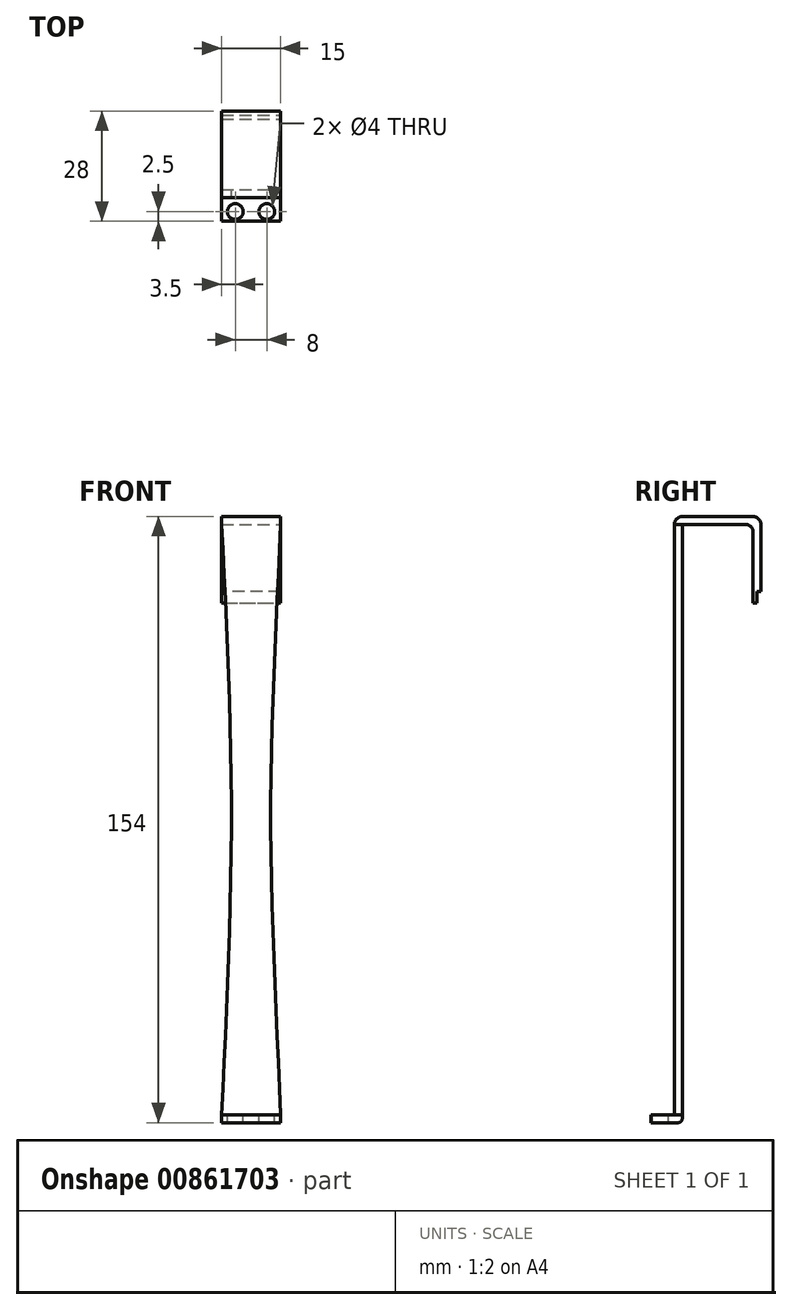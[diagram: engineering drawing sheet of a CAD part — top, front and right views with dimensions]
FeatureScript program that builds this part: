
annotation { "Feature Type Name" : "Feature", "Feature Type Description" : "" }
export const myFeature = defineFeature(function(context is Context, id is Id, definition is map)
    precondition{}
    {
        {
            var Q0;
            Q0=qCreatedBy(makeId("Front.planeOp"),FACE);
            var sketch = newSketch(context, id + "F0", { "sketchPlane" : qUnion([Q0])});
            skLineSegment(sketch, "E0.bottom", {"start": v(-7.5, 72.7) * mm, "end": v(7.5, 72.7) * mm});
            skLineSegment(sketch, "E0.top", {"start": v(-7.5, -77.3) * mm, "end": v(7.5, -77.3) * mm});
            skFitSpline(sketch, "E1", {"points": [v(-7.5, 72.7) * mm, v(-5, 0) * mm, v(-7.5, -77.3) * mm], "startDerivative": vector(7.76, -146.53) * mm, "endDerivative": vector(-7.68, -153.44) * mm});
            skFitSpline(sketch, "E2", {"points": [v(7.5, 72.7) * mm, v(5, 0) * mm, v(7.5, -77.3) * mm], "startDerivative": vector(-6.19, -146.53) * mm, "endDerivative": vector(6.12, -153.44) * mm});
            skSolve(sketch);
        }
        {
            var Q0;
            Q0 = qSketchRegion(id + "F0", true);
            extrude(context, id + "F1", {"entities" : qUnion([Q0]), "depth" : 2 * mm, "offsetDistance" : 25 * mm});
        }
        {
            var Q0;
            Q0=makeQuery(id+"F1.opExtrude","CAP_EDGE",EDGE,{"disambiguationData":[OSD([sQuery(id+"F0.wireOp",EDGE,"E0.bottom")])],"isStart":true});
            var Q1;
            Q1=makeQuery(id+"F1.opExtrude","CAP_EDGE",EDGE,{"disambiguationData":[OSD([sQuery(id+"F0.wireOp",EDGE,"E0.bottom")])],"isStart":false});
            cPlane(context, id + "F2", {"entities" : qUnion([Q0, Q1]), "cplaneType" : CPlaneType.LINE_ANGLE, "offset" : 25 * mm, "angle" : 0 * degree, "width" : 150 * mm, "height" : 150 * mm});
        }
        {
            var Q0;
            Q0=qCreatedBy(id+"F2.planeOp",FACE);
            var sketch = newSketch(context, id + "F3", { "sketchPlane" : qUnion([Q0])});
            skLineSegment(sketch, "E3.bottom", {"start": v(-7.5, -20) * mm, "end": v(7.5, -20) * mm});
            skLineSegment(sketch, "E3.top", {"start": v(-7.5, 2) * mm, "end": v(7.5, 2) * mm});
            skLineSegment(sketch, "E3.left", {"start": v(-7.5, -20) * mm, "end": v(-7.5, 2) * mm});
            skLineSegment(sketch, "E3.right", {"start": v(7.5, -20) * mm, "end": v(7.5, 2) * mm});
            skSolve(sketch);
        }
        {
            var Q0;
            Q0 = qSketchRegion(id + "F3", true);
            extrude(context, id + "F4", {"entities" : qUnion([Q0]), "operationType" : NewBodyOperationType.ADD, "oppositeDirection" : true, "depth" : 2 * mm, "offsetDistance" : 25 * mm});
        }
        {
            var Q0;
            Q0=makeQuery(id+"F4.opExtrude","CAP_EDGE",EDGE,{"disambiguationData":[OSD([sQuery(id+"F3.wireOp",EDGE,"E3.bottom")])],"isStart":false});
            var Q1;
            Q1=makeQuery(id+"F4.opExtrude","CAP_EDGE",EDGE,{"disambiguationData":[OSD([sQuery(id+"F3.wireOp",EDGE,"E3.bottom")])],"isStart":true});
            cPlane(context, id + "F5", {"entities" : qUnion([Q0, Q1]), "cplaneType" : CPlaneType.LINE_ANGLE, "offset" : 25 * mm, "angle" : 0 * degree, "width" : 150 * mm, "height" : 150 * mm});
        }
        {
            var Q0;
            Q0=qCreatedBy(id+"F5.planeOp",FACE);
            var sketch = newSketch(context, id + "F6", { "sketchPlane" : qUnion([Q0])});
            skLineSegment(sketch, "E4.bottom", {"start": v(7.5, 74.7) * mm, "end": v(-7.5, 74.7) * mm});
            skLineSegment(sketch, "E4.top", {"start": v(7.5, 52.7) * mm, "end": v(-7.5, 52.7) * mm});
            skLineSegment(sketch, "E4.left", {"start": v(7.5, 74.7) * mm, "end": v(7.5, 52.7) * mm});
            skLineSegment(sketch, "E4.right", {"start": v(-7.5, 74.7) * mm, "end": v(-7.5, 52.7) * mm});
            skSolve(sketch);
        }
        {
            var Q0;
            Q0 = qSketchRegion(id + "F6", true);
            extrude(context, id + "F7", {"entities" : qUnion([Q0]), "operationType" : NewBodyOperationType.ADD, "oppositeDirection" : true, "depth" : 2 * mm, "offsetDistance" : 25 * mm});
        }
        {
            var Q0;
            Q0=makeQuery(id+"F4.opExtrude","CAP_EDGE",EDGE,{"disambiguationData":[OSD([sQuery(id+"F3.wireOp",EDGE,"E3.top")])],"isStart":false});
            var Q1;
            Q1=makeQuery(id+"F4.opExtrude","CAP_EDGE",EDGE,{"disambiguationData":[OSD([sQuery(id+"F3.wireOp",EDGE,"E3.bottom")])],"isStart":false});
            var Q2;
            Q2=makeQuery(id+"F1.opExtrude","CAP_EDGE",EDGE,{"disambiguationData":[OSD([sQuery(id+"F0.wireOp",EDGE,"E0.bottom")])],"isStart":true});
            var Q3;
            Q3=makeQuery(id+"F7.boolean.opBoolean","INTERSECT",EDGE,{"derivedFrom":[makeQuery(id+"F4.opExtrude","CAP_FACE",FACE,{"disambiguationData":[OSD([sQuery(id+"F3.wireOp",EDGE,"E3.bottom"),sQuery(id+"F3.wireOp",EDGE,"E3.top"),sQuery(id+"F3.wireOp",EDGE,"E3.left"),sQuery(id+"F3.wireOp",EDGE,"E3.right")])],"isStart":true}),makeQuery(id+"F7.opExtrude","CAP_FACE",FACE,{"disambiguationData":[OSD([sQuery(id+"F6.wireOp",EDGE,"E4.bottom"),sQuery(id+"F6.wireOp",EDGE,"E4.top"),sQuery(id+"F6.wireOp",EDGE,"E4.left"),sQuery(id+"F6.wireOp",EDGE,"E4.right")])],"isStart":false})]});
            fillet(context, id + "F8", {"entities" : qUnion([Q0, Q1, Q2, Q3]), "radius" : 2 * mm, "tangentPropagation" : true, "allowEdgeOverflow" : false});
        }
        {
            var Q0;
            Q0=makeQuery(id+"F1.opExtrude","CAP_EDGE",EDGE,{"disambiguationData":[OSD([sQuery(id+"F0.wireOp",EDGE,"E0.top")])],"isStart":true});
            var Q1;
            Q1=makeQuery(id+"F1.opExtrude","CAP_EDGE",EDGE,{"disambiguationData":[OSD([sQuery(id+"F0.wireOp",EDGE,"E0.top")])],"isStart":false});
            cPlane(context, id + "F9", {"entities" : qUnion([Q0, Q1]), "cplaneType" : CPlaneType.LINE_ANGLE, "offset" : 25 * mm, "angle" : 0 * degree, "width" : 150 * mm, "height" : 150 * mm});
        }
        {
            var Q0;
            Q0=qCreatedBy(id+"F9.planeOp",FACE);
            var sketch = newSketch(context, id + "F10", { "sketchPlane" : qUnion([Q0])});
            skLineSegment(sketch, "E5.bottom", {"start": v(-7.5, 8) * mm, "end": v(-7.5, 8) * mm});
            skLineSegment(sketch, "E5.top", {"start": v(-7.5, 0) * mm, "end": v(-7.5, 0) * mm});
            skLineSegment(sketch, "E5.left", {"start": v(-7.5, 8) * mm, "end": v(-7.5, 0) * mm});
            skLineSegment(sketch, "E5.right", {"start": v(-7.5, 8) * mm, "end": v(-7.5, 0) * mm});
            skPoint(sketch, "E6", {"position": v(-4, 5.5) * mm});
            skPoint(sketch, "E7", {"position": v(4, 5.5) * mm});
            skCircle(sketch, "E8", {"center": v(-4, 5.5) * mm, "radius": 2 * mm});
            skCircle(sketch, "E9", {"center": v(4, 5.5) * mm, "radius": 2 * mm});
            skLineSegment(sketch, "E10.bottom", {"start": v(7.5, 8) * mm, "end": v(-7.5, 8) * mm});
            skLineSegment(sketch, "E10.top", {"start": v(7.5, 0) * mm, "end": v(-7.5, 0) * mm});
            skLineSegment(sketch, "E10.left", {"start": v(7.5, 8) * mm, "end": v(7.5, 0) * mm});
            skSolve(sketch);
        }
        {
            var Q0;
            Q0 = qSketchRegion(id + "F10", true);
            extrude(context, id + "F11", {"entities" : qUnion([Q0]), "operationType" : NewBodyOperationType.ADD, "depth" : 2 * mm, "offsetDistance" : 25 * mm});
        }
        {
            var Q0;
            Q0=makeQuery(id+"F11.opExtrude","CAP_EDGE",EDGE,{"disambiguationData":[OSD([sQuery(id+"F10.wireOp",EDGE,"E10.top")])],"isStart":false});
            var Q1;
            Q1=makeQuery(id+"F1.opExtrude","CAP_EDGE",EDGE,{"disambiguationData":[OSD([sQuery(id+"F0.wireOp",EDGE,"E0.top")])],"isStart":false});
            fillet(context, id + "F12", {"entities" : qUnion([Q0, Q1]), "radius" : 1 * mm, "tangentPropagation" : true, "allowEdgeOverflow" : false});
        }
        {
            var Q0;
            Q0=makeQuery(id+"F7.boolean.opBoolean","MERGE",FACE,{"derivedFrom":[makeQuery(id+"F4.opExtrude","SWEPT_FACE",FACE,{"disambiguationData":[OSD([sQuery(id+"F3.wireOp",EDGE,"E3.bottom")])]}),makeQuery(id+"F7.opExtrude","CAP_FACE",FACE,{"disambiguationData":[OSD([sQuery(id+"F6.wireOp",EDGE,"E4.bottom"),sQuery(id+"F6.wireOp",EDGE,"E4.top"),sQuery(id+"F6.wireOp",EDGE,"E4.left"),sQuery(id+"F6.wireOp",EDGE,"E4.right")])],"isStart":true})]});
            var sketch = newSketch(context, id + "F13", { "sketchPlane" : qUnion([Q0])});
            skLineSegment(sketch, "E11.bottom", {"start": v(-7.5, 52.7) * mm, "end": v(7.5, 52.7) * mm});
            skLineSegment(sketch, "E11.top", {"start": v(-7.5, 55.7) * mm, "end": v(7.5, 55.7) * mm});
            skLineSegment(sketch, "E11.left", {"start": v(-7.5, 52.7) * mm, "end": v(-7.5, 55.7) * mm});
            skLineSegment(sketch, "E11.right", {"start": v(7.5, 52.7) * mm, "end": v(7.5, 55.7) * mm});
            skSolve(sketch);
        }
        {
            var Q0;
            Q0 = qSketchRegion(id + "F13", true);
            extrude(context, id + "F14", {"entities" : qUnion([Q0]), "operationType" : NewBodyOperationType.REMOVE, "oppositeDirection" : true, "depth" : 1 * mm, "offsetDistance" : 25 * mm});
        }
    });
